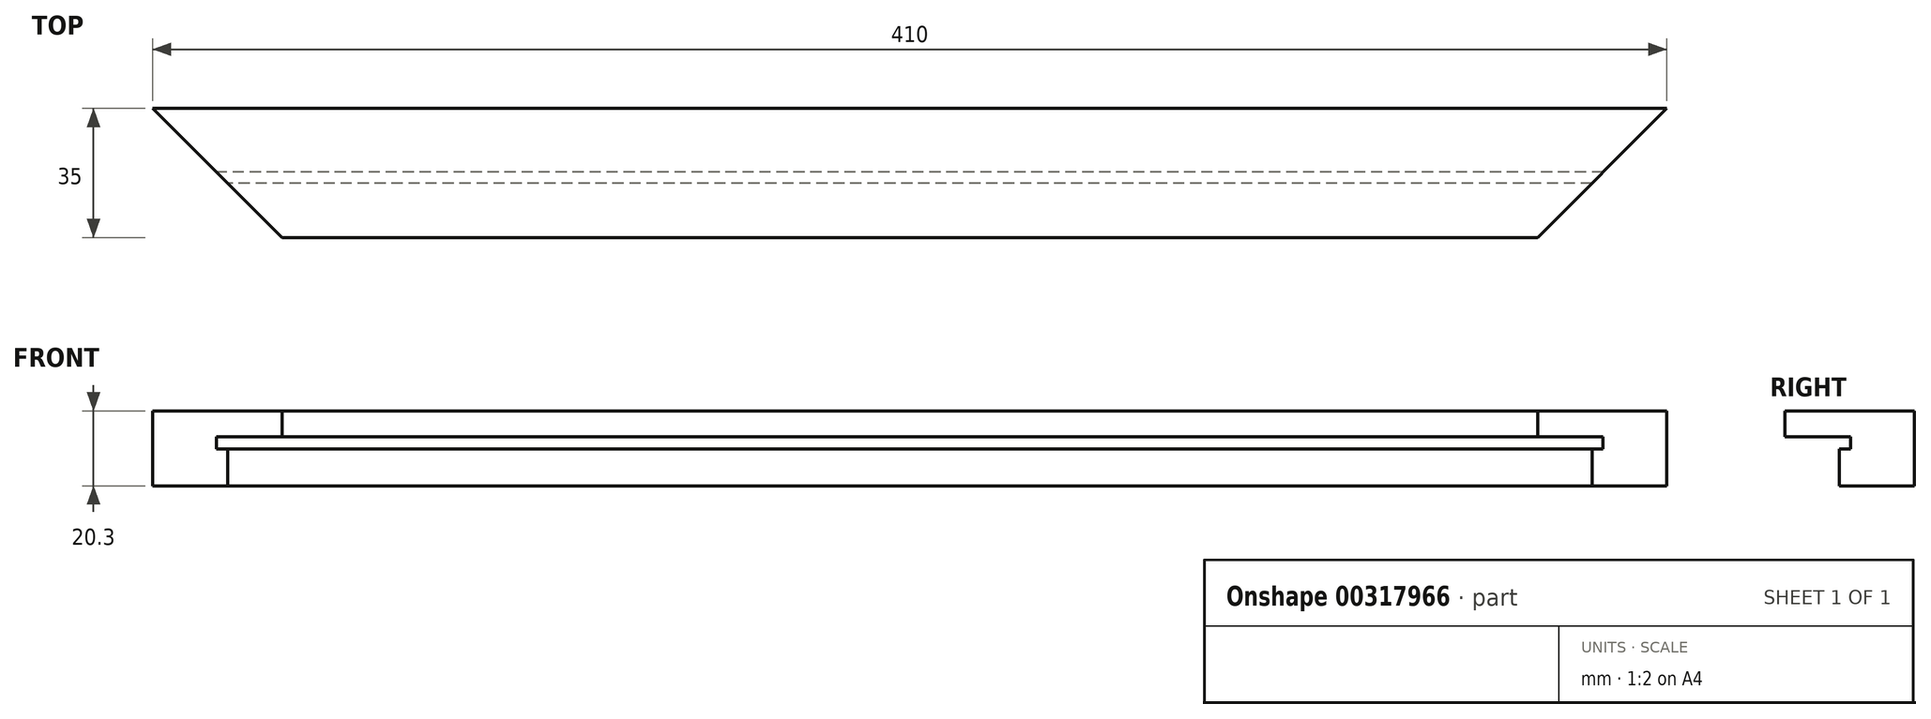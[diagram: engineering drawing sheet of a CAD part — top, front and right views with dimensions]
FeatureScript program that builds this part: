
annotation { "Feature Type Name" : "Feature", "Feature Type Description" : "" }
export const myFeature = defineFeature(function(context is Context, id is Id, definition is map)
    precondition{}
    {
        {
            var Q0;
            Q0=qCreatedBy(makeId("Right.planeOp"),FACE);
            var sketch = newSketch(context, id + "F0", { "sketchPlane" : qUnion([Q0])});
            skLineSegment(sketch, "E0", {"start": v(17.3, 10.3) * mm, "end": v(-17.7, 10.3) * mm});
            skLineSegment(sketch, "E1", {"start": v(-17.7, 10.3) * mm, "end": v(-17.7, 3.3) * mm});
            skLineSegment(sketch, "E2", {"start": v(-17.7, 3.3) * mm, "end": v(0, 3.3) * mm});
            skLineSegment(sketch, "E3", {"start": v(0, 3.3) * mm, "end": v(0, 0) * mm});
            skLineSegment(sketch, "E4", {"start": v(0, 0) * mm, "end": v(-3, 0) * mm});
            skLineSegment(sketch, "E5", {"start": v(-3, 0) * mm, "end": v(-3, -10) * mm});
            skLineSegment(sketch, "E6", {"start": v(17.3, 10.3) * mm, "end": v(17.3, -10) * mm});
            skLineSegment(sketch, "E7", {"start": v(17.3, -10) * mm, "end": v(-3, -10) * mm});
            skSolve(sketch);
        }
        {
            var Q0;
            Q0 = qSketchRegion(id + "F0", true);
            extrude(context, id + "F1", {"entities" : qUnion([Q0]), "endBound" : BoundingType.SYMMETRIC, "depth" : 410 * mm});
        }
        {
            var Q0;
            Q0=makeQuery(id+"F1.opExtrude","SWEPT_FACE",FACE,{"disambiguationData":[OSD([sQuery(id+"F0.wireOp",EDGE,"E0")])]});
            var sketch = newSketch(context, id + "F2", { "sketchPlane" : qUnion([Q0])});
            skLineSegment(sketch, "E8", {"start": v(-205, 17.3) * mm, "end": v(-170, -17.7) * mm});
            skLineSegment(sketch, "E9", {"start": v(-170, -17.7) * mm, "end": v(-205, -17.7) * mm});
            skLineSegment(sketch, "E10", {"start": v(-205, -17.7) * mm, "end": v(-205, 17.3) * mm});
            skLineSegment(sketch, "E11.MirrorCS", {"start": v(205, 17.3) * mm, "end": v(170, -17.7) * mm});
            skLineSegment(sketch, "E12.MirrorCS", {"start": v(205, -17.7) * mm, "end": v(205, 17.3) * mm});
            skLineSegment(sketch, "E13.MirrorCS", {"start": v(170, -17.7) * mm, "end": v(205, -17.7) * mm});
            skSolve(sketch);
        }
        {
            var Q0;
            Q0 = qSketchRegion(id + "F2", true);
            extrude(context, id + "F3", {"entities" : qUnion([Q0]), "operationType" : NewBodyOperationType.REMOVE, "oppositeDirection" : true, "depth" : 25.4 * mm});
        }
    });
